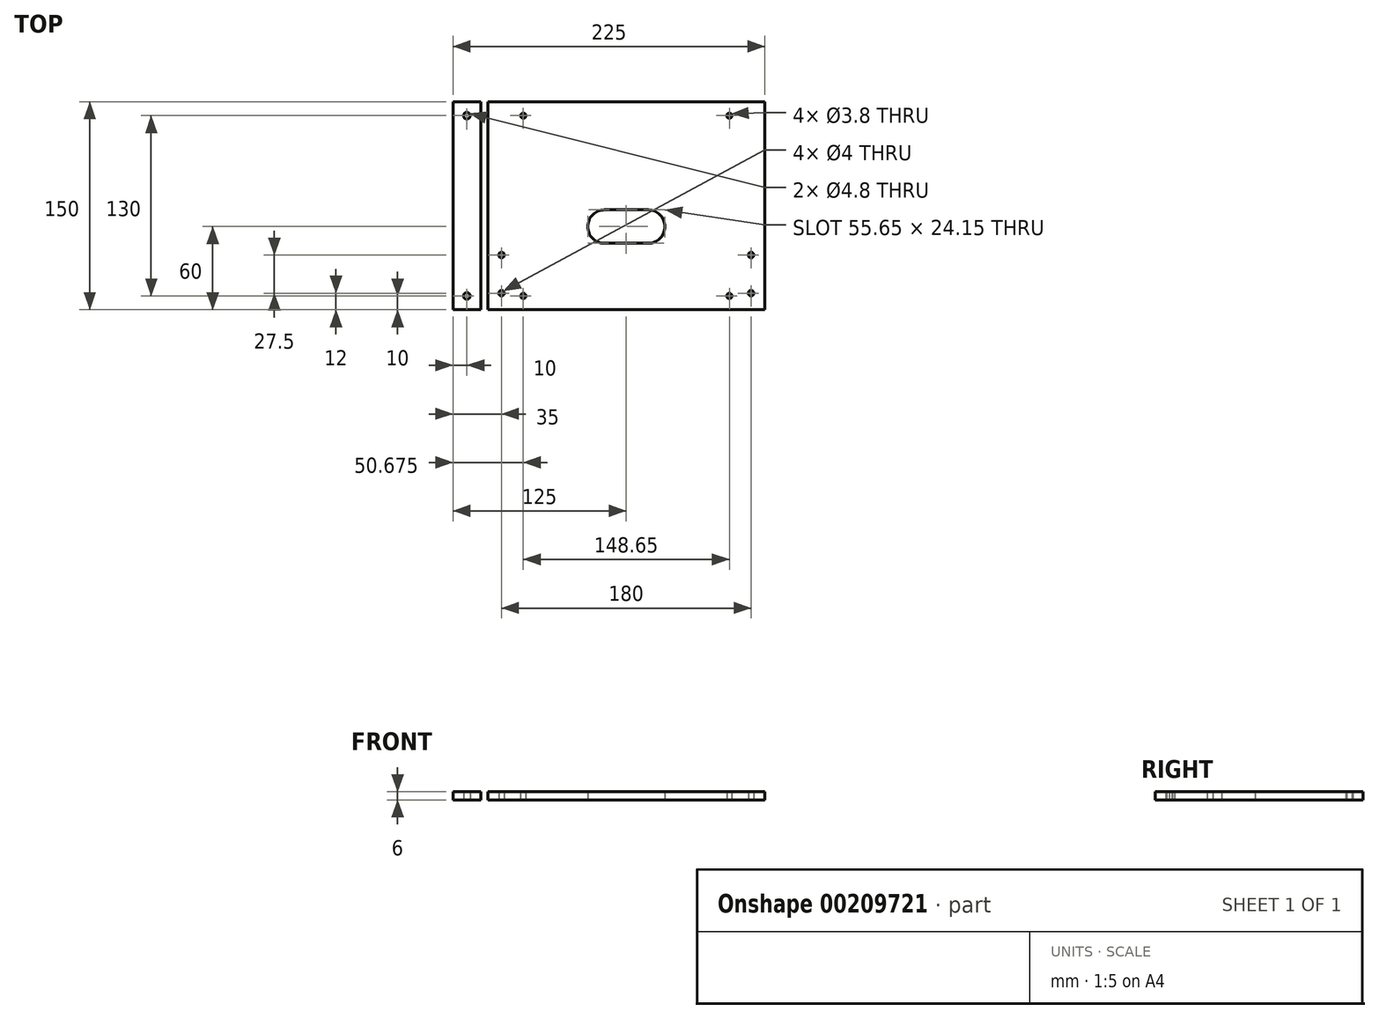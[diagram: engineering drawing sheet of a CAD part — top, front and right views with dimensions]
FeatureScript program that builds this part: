
annotation { "Feature Type Name" : "Feature", "Feature Type Description" : "" }
export const myFeature = defineFeature(function(context is Context, id is Id, definition is map)
    precondition{}
    {
        {
            var Q0;
            Q0=qCreatedBy(makeId("Top.planeOp"),FACE);
            var sketch = newSketch(context, id + "F0", { "sketchPlane" : qUnion([Q0])});
            skLineSegment(sketch, "E0.bottom", {"start": v(-15.75, -6.75) * mm, "end": v(15.75, -6.75) * mm});
            skLineSegment(sketch, "E0.top", {"start": v(-15.75, 6.75) * mm, "end": v(15.75, 6.75) * mm});
            skArc(sketch, "E1", {"start": v(-15.75, 6.75) * mm, "mid": v(-22.5, 0) * mm, "end": v(-15.75, -6.75) * mm});
            skArc(sketch, "E2", {"start": v(15.75, -6.75) * mm, "mid": v(22.5, 0) * mm, "end": v(15.75, 6.75) * mm});
            skLineSegment(sketch, "E3", {"start": v(-124.64, -10.5) * mm, "end": v(111.46, -10.5) * mm});
            skSolve(sketch);
        }
        {
            var Q0;
            Q0=qCreatedBy(makeId("Top.planeOp"),FACE);
            var sketch = newSketch(context, id + "F1", { "sketchPlane" : qUnion([Q0])});
            skCircle(sketch, "E4", {"center": v(-8.9, 3.58) * mm, "radius": 3.17 * mm});
            skCircle(sketch, "E5", {"center": v(-8.9, 3.58) * mm, "radius": 8.5 * mm});
            skSolve(sketch);
        }
        {
            var Q0;
            Q0=qCreatedBy(makeId("Top.planeOp"),FACE);
            var sketch = newSketch(context, id + "F2", { "sketchPlane" : qUnion([Q0])});
            skLineSegment(sketch, "E6", {"start": v(-64.33, 90) * mm, "end": v(-64.32, -60) * mm, "construction": true});
            skCircle(sketch, "E7", {"center": v(-6.83, 3.34) * mm, "radius": 3.17 * mm, "construction": true});
            skSolve(sketch);
        }
        {
            var Q0;
            Q0=qCreatedBy(makeId("Top.planeOp"),FACE);
            var sketch = newSketch(context, id + "F3", { "sketchPlane" : qUnion([Q0])});
            skLineSegment(sketch, "E8.bottom", {"start": v(-15.75, 12.08) * mm, "end": v(15.75, 12.08) * mm});
            skLineSegment(sketch, "E8.top", {"start": v(-15.75, -12.08) * mm, "end": v(15.75, -12.08) * mm});
            skArc(sketch, "E9", {"start": v(-15.75, 12.08) * mm, "mid": v(-27.83, 0) * mm, "end": v(-15.75, -12.08) * mm});
            skArc(sketch, "E10", {"start": v(15.75, -12.08) * mm, "mid": v(27.83, 0) * mm, "end": v(15.75, 12.08) * mm});
            skLineSegment(sketch, "E11.bottom", {"start": v(-100, -60) * mm, "end": v(100, -60) * mm});
            skLineSegment(sketch, "E11.top", {"start": v(-100, 90) * mm, "end": v(100, 90) * mm});
            skLineSegment(sketch, "E11.left", {"start": v(-100, -60) * mm, "end": v(-100, 90) * mm});
            skLineSegment(sketch, "E11.right", {"start": v(100, -60) * mm, "end": v(100, 90) * mm});
            skCircle(sketch, "E12", {"center": v(-90, -48) * mm, "radius": 2 * mm});
            skCircle(sketch, "E13", {"center": v(-90, -20.5) * mm, "radius": 2 * mm});
            skCircle(sketch, "E14", {"center": v(90, -20.5) * mm, "radius": 2 * mm});
            skCircle(sketch, "E15", {"center": v(90, -48) * mm, "radius": 2 * mm});
            skCircle(sketch, "E16", {"center": v(-74.32, -50) * mm, "radius": 1.9 * mm});
            skCircle(sketch, "E17", {"center": v(-74.33, 80) * mm, "radius": 1.9 * mm});
            skCircle(sketch, "E18.MirrorC", {"center": v(74.33, 80) * mm, "radius": 1.9 * mm});
            skCircle(sketch, "E19.MirrorC", {"center": v(74.32, -50) * mm, "radius": 1.9 * mm});
            skSolve(sketch);
        }
        {
            var Q0;
            Q0=qCreatedBy(makeId("Top.planeOp"),FACE);
            var sketch = newSketch(context, id + "F4", { "sketchPlane" : qUnion([Q0])});
            skLineSegment(sketch, "E20.bottom", {"start": v(-105, 90) * mm, "end": v(-125, 90) * mm});
            skLineSegment(sketch, "E20.top", {"start": v(-105, -60) * mm, "end": v(-125, -60) * mm});
            skLineSegment(sketch, "E20.left", {"start": v(-105, 90) * mm, "end": v(-105, -60) * mm});
            skLineSegment(sketch, "E20.right", {"start": v(-125, 90) * mm, "end": v(-125, -60) * mm});
            skLineSegment(sketch, "E21", {"start": v(-115, -60) * mm, "end": v(-115, 90) * mm, "construction": true});
            skCircle(sketch, "E22", {"center": v(-115, 80) * mm, "radius": 2.4 * mm});
            skCircle(sketch, "E23", {"center": v(-115, -50) * mm, "radius": 2.4 * mm});
            skLineSegment(sketch, "E24", {"start": v(-115, 80) * mm, "end": v(-74.33, 80) * mm, "construction": true});
            skLineSegment(sketch, "E25", {"start": v(-115, -50) * mm, "end": v(-74.32, -50) * mm, "construction": true});
            skSolve(sketch);
        }
        {
            var Q0;
            Q0=makeQuery(id+"F4.imprint","IMPRINT",FACE,{"disambiguationData":[TD([[makeQuery(id+"F4.imprint","IMPRINT",EDGE,{"derivedFrom":sQuery(id+"F4.wireOp",EDGE,"E20.bottom")}),1.0]])]});
            var Q1;
            Q1=makeQuery(id+"F3.imprint","IMPRINT",FACE,{"disambiguationData":[TD([[makeQuery(id+"F3.imprint","IMPRINT",EDGE,{"derivedFrom":sQuery(id+"F3.wireOp",EDGE,"E8.bottom")}),1.0]])]});
            var Q2;
            Q2=makeQuery(id+"FfPUDYlGDrxDoak_0.1.F4.imprint","IMPRINT",FACE,{"disambiguationData":[TD([[makeQuery(id+"FfPUDYlGDrxDoak_0.1.F4.imprint","IMPRINT",EDGE,{"derivedFrom":sQuery(id+"FfPUDYlGDrxDoak_0.1.F4.wireOp",EDGE,"E20.bottom")}),1.0]])]});
            extrude(context, id + "F5", {"entities" : qUnion([Q0, Q1, Q2]), "depth" : 6 * mm});
        }
    });
